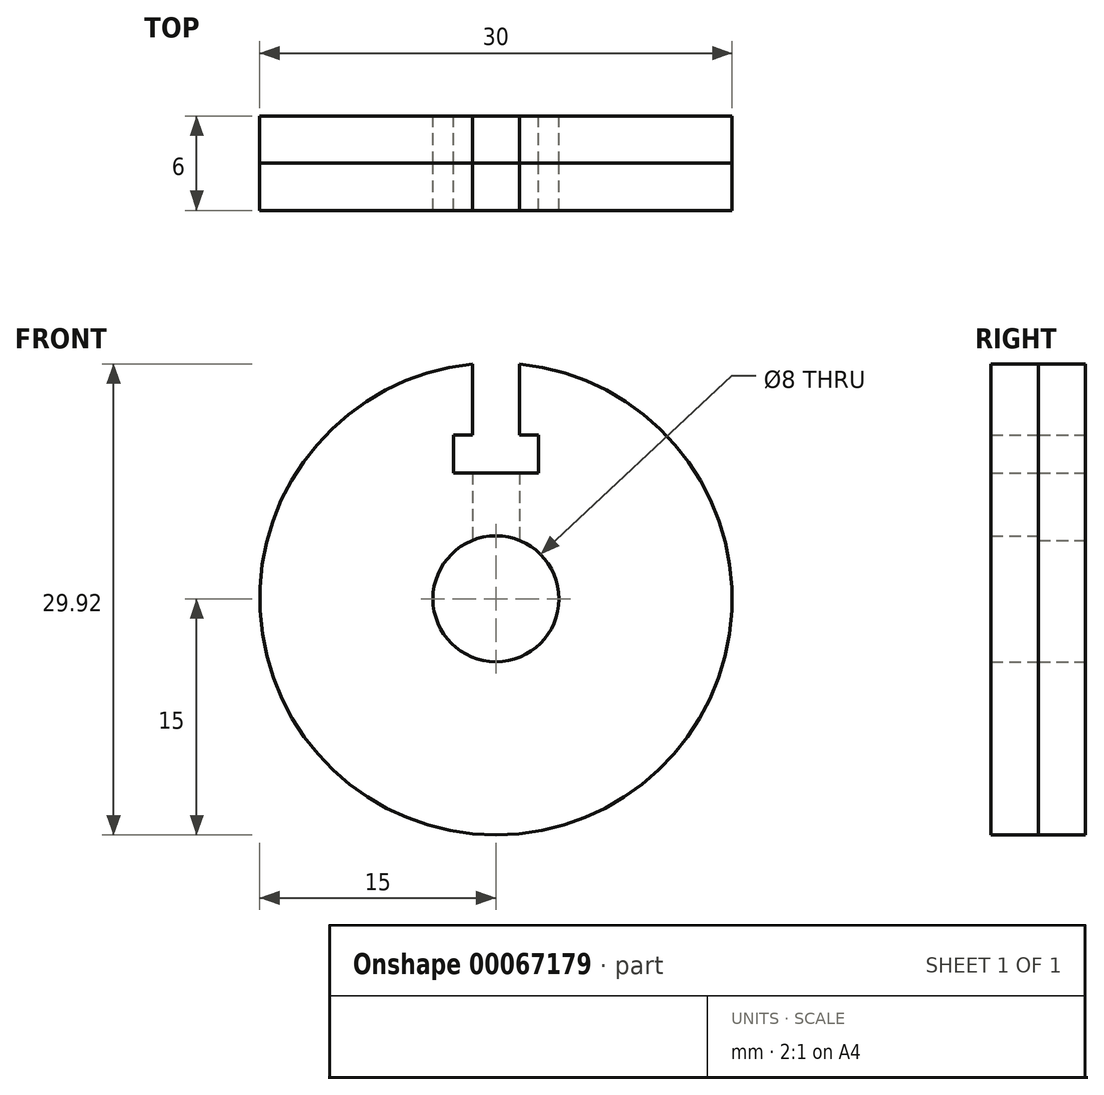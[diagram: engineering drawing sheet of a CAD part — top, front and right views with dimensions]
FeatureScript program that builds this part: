
annotation { "Feature Type Name" : "Feature", "Feature Type Description" : "" }
export const myFeature = defineFeature(function(context is Context, id is Id, definition is map)
    precondition{}
    {
        {
            var Q0;
            Q0=qCreatedBy(makeId("Front.planeOp"),FACE);
            var sketch = newSketch(context, id + "F0", { "sketchPlane" : qUnion([Q0])});
            skCircle(sketch, "E0", {"center": v(0, 0) * mm, "radius": 15 * mm});
            skCircle(sketch, "E1", {"center": v(0, 0) * mm, "radius": 4 * mm});
            skLineSegment(sketch, "E2", {"start": v(-1.5, 14.92) * mm, "end": v(-1.5, 10.4) * mm});
            skLineSegment(sketch, "E3", {"start": v(-1.5, 10.4) * mm, "end": v(-2.7, 10.4) * mm});
            skLineSegment(sketch, "E4", {"start": v(-2.7, 10.4) * mm, "end": v(-2.7, 8) * mm});
            skLineSegment(sketch, "E5", {"start": v(-2.7, 8) * mm, "end": v(-1.5, 8) * mm});
            skLineSegment(sketch, "E6", {"start": v(-1.5, 8) * mm, "end": v(-1.5, 3.7) * mm});
            skLineSegment(sketch, "E7", {"start": v(0, 0) * mm, "end": v(0, 9.62) * mm, "construction": true});
            skLineSegment(sketch, "E8", {"start": v(-1.5, 3.7) * mm, "end": v(0, 3.7) * mm});
            skLineSegment(sketch, "E9.MirrorCS", {"start": v(1.5, 3.7) * mm, "end": v(0, 3.7) * mm});
            skLineSegment(sketch, "E10.MirrorCS", {"start": v(1.5, 8) * mm, "end": v(1.5, 3.7) * mm});
            skLineSegment(sketch, "E11.MirrorCS", {"start": v(2.7, 8) * mm, "end": v(1.5, 8) * mm});
            skLineSegment(sketch, "E12.MirrorCS", {"start": v(2.7, 10.4) * mm, "end": v(2.7, 8) * mm});
            skLineSegment(sketch, "E13.MirrorCS", {"start": v(1.5, 10.4) * mm, "end": v(2.7, 10.4) * mm});
            skLineSegment(sketch, "E14.MirrorCS", {"start": v(1.5, 14.92) * mm, "end": v(1.5, 10.4) * mm});
            skSolve(sketch);
        }
        {
            var Q0;
            {var subQ2=sQuery(id+"F0.wireOp",EDGE,"E2");Q0=makeQuery(id+"F0.imprint","IMPRINT",FACE,{"disambiguationData":[TD([[makeQuery(id+"F0.imprint","IMPRINT",EDGE,{"derivedFrom":subQ2}),-1.0]])]});}
            extrude(context, id + "F1", {"entities" : qUnion([Q0]), "depth" : 3 * mm});
        }
        {
            var Q0;
            Q0=makeQuery(id+"F1.opExtrude","CAP_FACE",FACE,{"disambiguationData":[OSD([sQuery(id+"F0.wireOp",EDGE,"E0"),sQuery(id+"F0.wireOp",EDGE,"E1"),sQuery(id+"F0.wireOp",EDGE,"E2"),sQuery(id+"F0.wireOp",EDGE,"E3"),sQuery(id+"F0.wireOp",EDGE,"E4"),sQuery(id+"F0.wireOp",EDGE,"E5"),sQuery(id+"F0.wireOp",EDGE,"E6"),sQuery(id+"F0.wireOp",EDGE,"E10.MirrorCS"),sQuery(id+"F0.wireOp",EDGE,"E11.MirrorCS"),sQuery(id+"F0.wireOp",EDGE,"E12.MirrorCS"),sQuery(id+"F0.wireOp",EDGE,"E13.MirrorCS"),sQuery(id+"F0.wireOp",EDGE,"E14.MirrorCS")])],"isStart":false});
            var sketch = newSketch(context, id + "F2", { "sketchPlane" : qUnion([Q0])});
            skCircle(sketch, "E15", {"center": v(0, 0) * mm, "radius": 10 * mm});
            skCircle(sketch, "E16", {"center": v(0, 0) * mm, "radius": 4 * mm});
            skPoint(sketch, "E17.0", {"position": v(-2.7, 10.4) * mm});
            skLineSegment(sketch, "E17.1", {"start": v(-1.5, 10.4) * mm, "end": v(-2.7, 10.4) * mm});
            skLineSegment(sketch, "E17.2", {"start": v(-2.7, 8) * mm, "end": v(-1.5, 8) * mm});
            skLineSegment(sketch, "E17.3", {"start": v(-2.7, 10.4) * mm, "end": v(-2.7, 8) * mm});
            skLineSegment(sketch, "E17.4", {"start": v(2.7, 10.4) * mm, "end": v(2.7, 8) * mm});
            skLineSegment(sketch, "E17.5", {"start": v(1.5, 10.4) * mm, "end": v(2.7, 10.4) * mm});
            skLineSegment(sketch, "E17.6", {"start": v(2.7, 8) * mm, "end": v(1.5, 8) * mm});
            skLineSegment(sketch, "E18", {"start": v(-1.5, 8) * mm, "end": v(1.5, 8) * mm});
            skLineSegment(sketch, "E19", {"start": v(1.5, 10.4) * mm, "end": v(-1.5, 10.4) * mm});
            skSolve(sketch);
        }
        {
            var Q0;
            Q0=makeQuery(id+"F2.imprint","IMPRINT",FACE,{"disambiguationData":[TD([[makeQuery(id+"F2.imprint","IMPRINT",EDGE,{"derivedFrom":sQuery(id+"F2.wireOp",EDGE,"E17.1")}),-1.0]])]});
            var Q1;
            Q1=makeQuery(id+"F2.imprint","IMPRINT",FACE,{"disambiguationData":[TD([[makeQuery(id+"F2.imprint","IMPRINT",EDGE,{"derivedFrom":sQuery(id+"F2.wireOp",EDGE,"E18")}),-1.0]])]});
            var Q2;
            {var subQ0=sQuery(id+"F2.wireOp",EDGE,"E16");var subQ1=makeQuery(id+"F2.imprint","INTERSECT",VERTEX,{"derivedFrom":[makeQuery(id+"F1.opExtrude","CAP_EDGE",EDGE,{"disambiguationData":[OSD([sQuery(id+"F0.wireOp",EDGE,"E6")])],"isStart":false}),subQ0]});Q2=makeQuery(id+"F2.imprint","IMPRINT",FACE,{"disambiguationData":[TD([[makeQuery(id+"F2.imprint","IMPRINT",EDGE,{"disambiguationData":[TD([[subQ1,1.0]])],"derivedFrom":subQ0}),1.0]])]});}
            var Q3;
            Q3=makeQuery(id+"F2.imprint","IMPRINT",FACE,{"disambiguationData":[TD([[makeQuery(id+"F2.imprint","IMPRINT",EDGE,{"derivedFrom":sQuery(id+"F2.wireOp",EDGE,"E19")}),-1.0]])]});
            var Q4;
            {var subQ1=sQuery(id+"F2.wireOp",EDGE,"E17.2");Q4=makeQuery(id+"F2.imprint","IMPRINT",FACE,{"disambiguationData":[TD([[makeQuery(id+"F2.imprint","IMPRINT",EDGE,{"derivedFrom":subQ1}),-1.0]])]});}
            extrude(context, id + "F3", {"entities" : qUnion([Q0, Q1, Q2, Q3, Q4]), "depth" : 3 * mm});
        }
        {
            var Q0;
            {var subQ0=sQuery(id+"F2.wireOp",EDGE,"E16");var subQ1=makeQuery(id+"F2.imprint","INTERSECT",VERTEX,{"derivedFrom":[makeQuery(id+"F1.opExtrude","CAP_EDGE",EDGE,{"disambiguationData":[OSD([sQuery(id+"F0.wireOp",EDGE,"E6")])],"isStart":false}),subQ0]});Q0=makeQuery(id+"F2.imprint","IMPRINT",FACE,{"disambiguationData":[TD([[makeQuery(id+"F2.imprint","IMPRINT",EDGE,{"disambiguationData":[TD([[subQ1,1.0]])],"derivedFrom":subQ0}),1.0]])]});}
            extrude(context, id + "F4", {"entities" : qUnion([Q0]), "operationType" : NewBodyOperationType.REMOVE, "depth" : 25 * mm});
        }
    });
